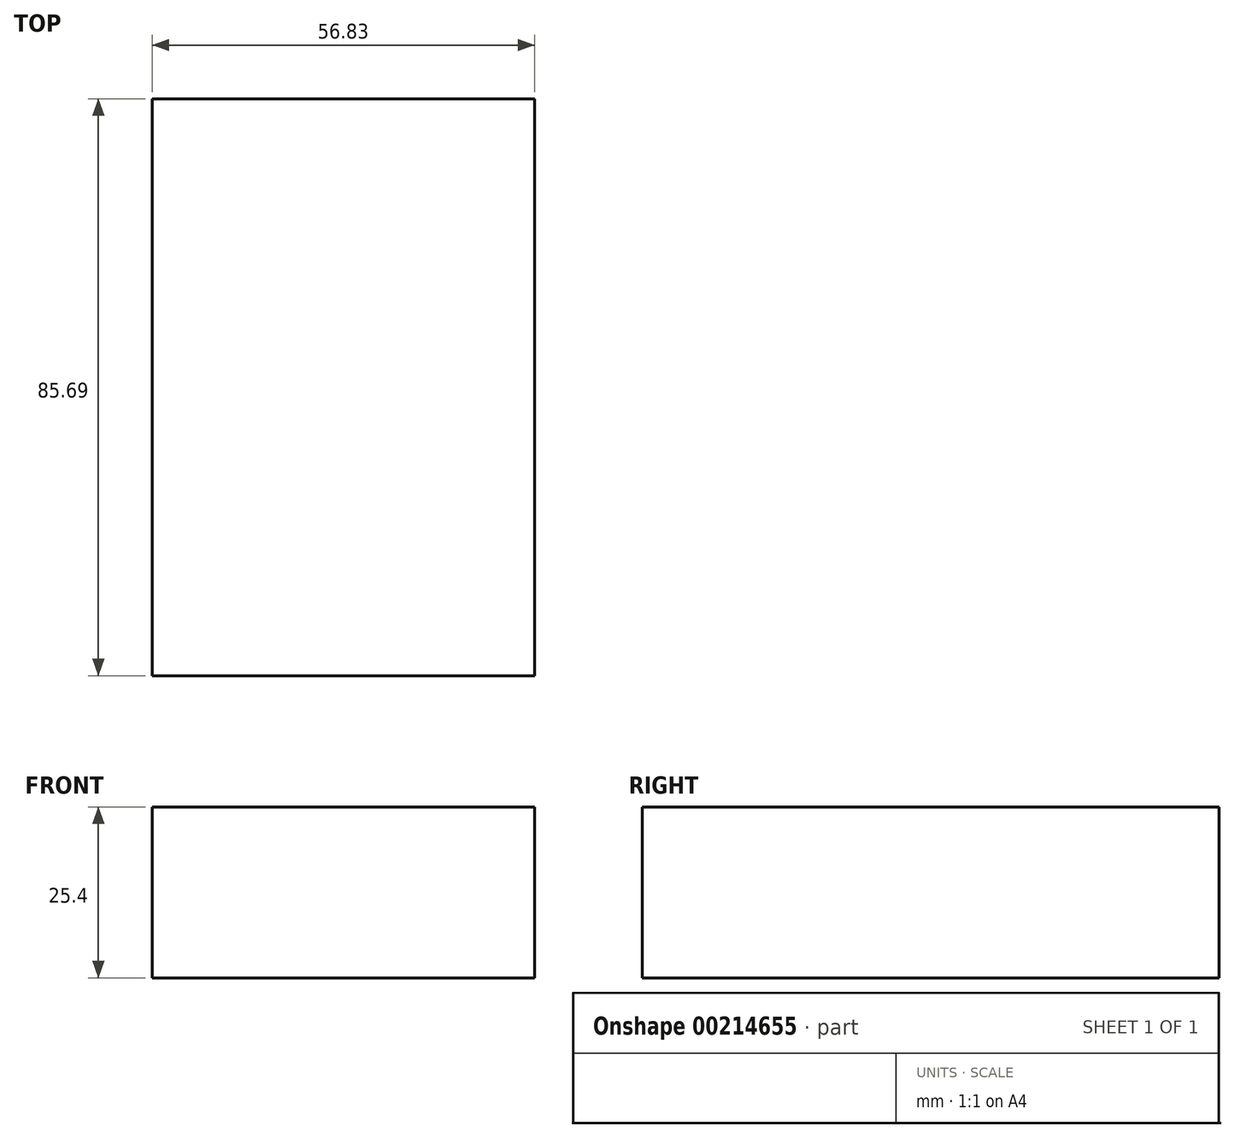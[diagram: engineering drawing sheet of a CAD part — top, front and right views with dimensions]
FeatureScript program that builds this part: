
annotation { "Feature Type Name" : "Feature", "Feature Type Description" : "" }
export const myFeature = defineFeature(function(context is Context, id is Id, definition is map)
    precondition{}
    {
        {
            var Q0;
            Q0=qCreatedBy(makeId("Top.planeOp"),FACE);
            var sketch = newSketch(context, id + "F0", { "sketchPlane" : qUnion([Q0])});
            skLineSegment(sketch, "E0", {"start": v(-66.16, 59.02) * mm, "end": v(-9.33, 59.02) * mm});
            skLineSegment(sketch, "E1", {"start": v(-9.33, 59.02) * mm, "end": v(-9.33, -26.67) * mm});
            skLineSegment(sketch, "E2", {"start": v(-9.33, -26.67) * mm, "end": v(-66.16, -26.67) * mm});
            skLineSegment(sketch, "E3", {"start": v(-66.16, -26.67) * mm, "end": v(-66.16, 59.02) * mm});
            skLineSegment(sketch, "E4", {"start": v(6.41, 59.02) * mm, "end": v(60.04, 59.02) * mm});
            skLineSegment(sketch, "E5", {"start": v(60.04, 59.02) * mm, "end": v(60.04, -26.67) * mm});
            skLineSegment(sketch, "E6", {"start": v(58.59, -26.96) * mm, "end": v(6.41, -26.67) * mm});
            skLineSegment(sketch, "E7", {"start": v(6.41, -26.67) * mm, "end": v(6.41, 59.02) * mm});
            skLineSegment(sketch, "E8", {"start": v(-66.16, -42.4) * mm, "end": v(-66.16, -70.85) * mm});
            skLineSegment(sketch, "E9", {"start": v(-65.6, -70.85) * mm, "end": v(60.04, -70.85) * mm});
            skLineSegment(sketch, "E10", {"start": v(58.43, -72.45) * mm, "end": v(58.43, -42.4) * mm});
            skLineSegment(sketch, "E11", {"start": v(58.43, -42.4) * mm, "end": v(-66.16, -42.4) * mm});
            skSolve(sketch);
        }
        {
            var Q0;
            Q0=qCreatedBy(makeId("Top.planeOp"),FACE);
            var sketch = newSketch(context, id + "F1", { "sketchPlane" : qUnion([Q0])});
            skSolve(sketch);
        }
        {
            var Q0;
            Q0 = qSketchRegion(id + "F1", true);
            var Q1;
            Q1=makeQuery(id+"F0.imprint","IMPRINT",FACE,{"disambiguationData":[TD([[makeQuery(id+"F0.imprint","IMPRINT",EDGE,{"derivedFrom":sQuery(id+"F0.wireOp",EDGE,"E0")}),-1.0]])]});
            extrude(context, id + "F2", {"entities" : qUnion([Q0, Q1]), "depth" : 25.4 * mm});
        }
    });
